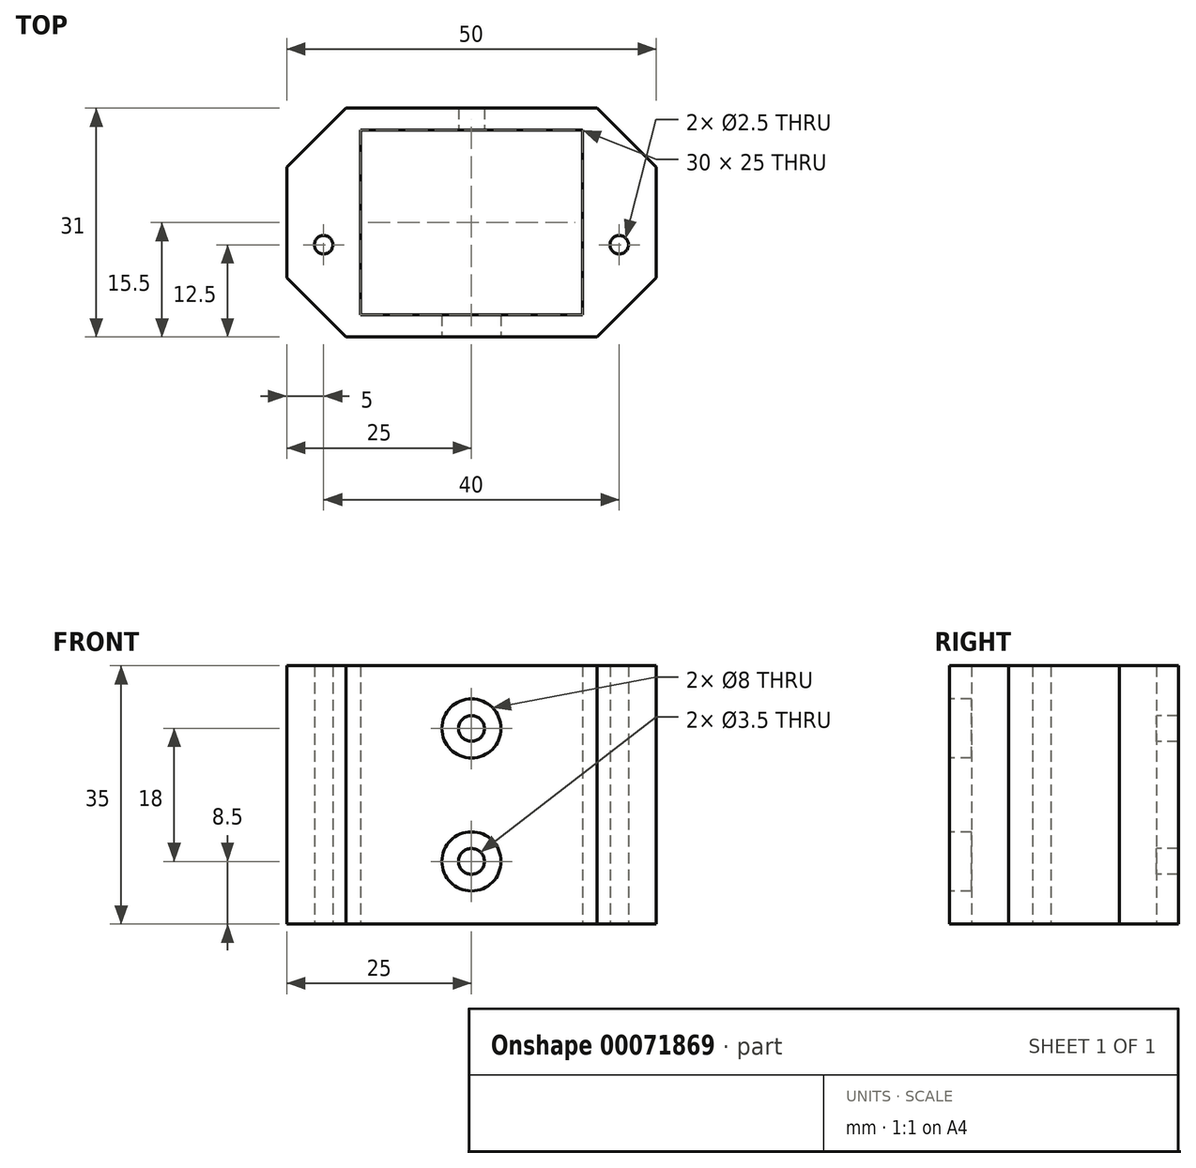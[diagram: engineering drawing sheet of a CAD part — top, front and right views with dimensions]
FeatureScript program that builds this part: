
annotation { "Feature Type Name" : "Feature", "Feature Type Description" : "" }
export const myFeature = defineFeature(function(context is Context, id is Id, definition is map)
    precondition{}
    {
        {
            var Q0;
            Q0=qCreatedBy(makeId("Top.planeOp"),FACE);
            var sketch = newSketch(context, id + "F0", { "sketchPlane" : qUnion([Q0])});
            skLineSegment(sketch, "E0.rect.bottom", {"start": v(15, 12.5) * mm, "end": v(-15, 12.5) * mm});
            skLineSegment(sketch, "E0.rect.top", {"start": v(15, -12.5) * mm, "end": v(-15, -12.5) * mm});
            skLineSegment(sketch, "E0.rect.left", {"start": v(15, 12.5) * mm, "end": v(15, -12.5) * mm});
            skLineSegment(sketch, "E0.rect.right", {"start": v(-15, 12.5) * mm, "end": v(-15, -12.5) * mm});
            skPoint(sketch, "E0.rect.middle", {"position": v(0, 0) * mm});
            skLineSegment(sketch, "E1.rect.bottom", {"start": v(25, 15.5) * mm, "end": v(-25, 15.5) * mm});
            skLineSegment(sketch, "E1.rect.top", {"start": v(25, -15.5) * mm, "end": v(-25, -15.5) * mm});
            skLineSegment(sketch, "E1.rect.left", {"start": v(25, 15.5) * mm, "end": v(25, -15.5) * mm});
            skLineSegment(sketch, "E1.rect.right", {"start": v(-25, 15.5) * mm, "end": v(-25, -15.5) * mm});
            skSolve(sketch);
        }
        {
            var Q0;
            Q0=makeQuery(id+"F0.imprint","IMPRINT",FACE,{"disambiguationData":[TD([[makeQuery(id+"F0.imprint","IMPRINT",EDGE,{"derivedFrom":sQuery(id+"F0.wireOp",EDGE,"E0.rect.bottom")}),-1.0]])]});
            extrude(context, id + "F1", {"entities" : qUnion([Q0]), "depth" : 35 * mm});
        }
        {
            var Q0;
            Q0=makeQuery(id+"F1.opExtrude","SWEPT_FACE",FACE,{"disambiguationData":[OSD([sQuery(id+"F0.wireOp",EDGE,"E1.rect.top")])]});
            var sketch = newSketch(context, id + "F2", { "sketchPlane" : qUnion([Q0])});
            skLineSegment(sketch, "E2", {"start": v(0, 0) * mm, "end": v(0, 35) * mm, "construction": true});
            skPoint(sketch, "E3", {"position": v(0, 17.5) * mm});
            skPoint(sketch, "E4", {"position": v(0, 8.5) * mm});
            skPoint(sketch, "E5", {"position": v(0, 26.5) * mm});
            skSolve(sketch);
        }
        {
            var Q0;
            Q0=sQuery(id+"F2.wireOp",VERTEX,"E5");
            var Q1;
            Q1=sQuery(id+"F2.wireOp",VERTEX,"E4");
            var Q2;
            Q2=makeQuery(id+"F1.opExtrude","SWEPT_BODY",BODY,{"disambiguationData":[OSD([sQuery(id+"F0.wireOp",EDGE,"E0.rect.bottom"),sQuery(id+"F0.wireOp",EDGE,"E0.rect.top"),sQuery(id+"F0.wireOp",EDGE,"E0.rect.left"),sQuery(id+"F0.wireOp",EDGE,"E0.rect.right"),sQuery(id+"F0.wireOp",EDGE,"E1.rect.bottom"),sQuery(id+"F0.wireOp",EDGE,"E1.rect.top"),sQuery(id+"F0.wireOp",EDGE,"E1.rect.left"),sQuery(id+"F0.wireOp",EDGE,"E1.rect.right")])]});
            hole(context, id + "F3", {"style" : HoleStyle.C_BORE, "holeDiameter" : 3.5 * mm, "cBoreDiameter" : 8 * mm, "cBoreDepth" : 5 * mm, "endStyle" : HoleEndStyle.THROUGH, "locations" : qUnion([Q0, Q1]), "scope" : qUnion([Q2])});
        }
        {
            var Q0;
            Q0=makeQuery(id+"F1.opExtrude","CAP_FACE",FACE,{"disambiguationData":[OSD([sQuery(id+"F0.wireOp",EDGE,"E0.rect.bottom"),sQuery(id+"F0.wireOp",EDGE,"E0.rect.top"),sQuery(id+"F0.wireOp",EDGE,"E0.rect.left"),sQuery(id+"F0.wireOp",EDGE,"E0.rect.right"),sQuery(id+"F0.wireOp",EDGE,"E1.rect.bottom"),sQuery(id+"F0.wireOp",EDGE,"E1.rect.top"),sQuery(id+"F0.wireOp",EDGE,"E1.rect.left"),sQuery(id+"F0.wireOp",EDGE,"E1.rect.right")])],"isStart":true});
            var sketch = newSketch(context, id + "F4", { "sketchPlane" : qUnion([Q0])});
            skPoint(sketch, "E6", {"position": v(-20, 3) * mm});
            skPoint(sketch, "E7.MirrorP", {"position": v(20, 3) * mm});
            skSolve(sketch);
        }
        {
            var Q0;
            Q0=sQuery(id+"F4.wireOp",VERTEX,"E6");
            var Q1;
            Q1=sQuery(id+"F4.wireOp",VERTEX,"E7.MirrorP");
            var Q2;
            Q2=makeQuery(id+"F1.opExtrude","SWEPT_BODY",BODY,{"disambiguationData":[OSD([sQuery(id+"F0.wireOp",EDGE,"E0.rect.bottom"),sQuery(id+"F0.wireOp",EDGE,"E0.rect.top"),sQuery(id+"F0.wireOp",EDGE,"E0.rect.left"),sQuery(id+"F0.wireOp",EDGE,"E0.rect.right"),sQuery(id+"F0.wireOp",EDGE,"E1.rect.bottom"),sQuery(id+"F0.wireOp",EDGE,"E1.rect.top"),sQuery(id+"F0.wireOp",EDGE,"E1.rect.left"),sQuery(id+"F0.wireOp",EDGE,"E1.rect.right")])]});
            hole(context, id + "F5", {"style" : HoleStyle.SIMPLE, "holeDiameter" : 2.5 * mm, "endStyle" : HoleEndStyle.THROUGH, "locations" : qUnion([Q0, Q1]), "scope" : qUnion([Q2])});
        }
        {
            var Q0;
            Q0=makeQuery(id+"F1.opExtrude","SWEPT_EDGE",EDGE,{"disambiguationData":[OSD([sQuery(id+"F0.wireOp",EDGE,"E1.rect.top"),sQuery(id+"F0.wireOp",EDGE,"E1.rect.left")])]});
            var Q1;
            Q1=makeQuery(id+"F1.opExtrude","SWEPT_EDGE",EDGE,{"disambiguationData":[OSD([sQuery(id+"F0.wireOp",EDGE,"E1.rect.top"),sQuery(id+"F0.wireOp",EDGE,"E1.rect.right")])]});
            var Q2;
            Q2=makeQuery(id+"F1.opExtrude","SWEPT_EDGE",EDGE,{"disambiguationData":[OSD([sQuery(id+"F0.wireOp",EDGE,"E1.rect.bottom"),sQuery(id+"F0.wireOp",EDGE,"E1.rect.right")])]});
            var Q3;
            Q3=makeQuery(id+"F1.opExtrude","SWEPT_EDGE",EDGE,{"disambiguationData":[OSD([sQuery(id+"F0.wireOp",EDGE,"E1.rect.bottom"),sQuery(id+"F0.wireOp",EDGE,"E1.rect.left")])]});
            chamfer(context, id + "F6", {"entities" : qUnion([Q0, Q1, Q2, Q3]), "width" : 8 * mm, "tangentPropagation" : true});
        }
    });
